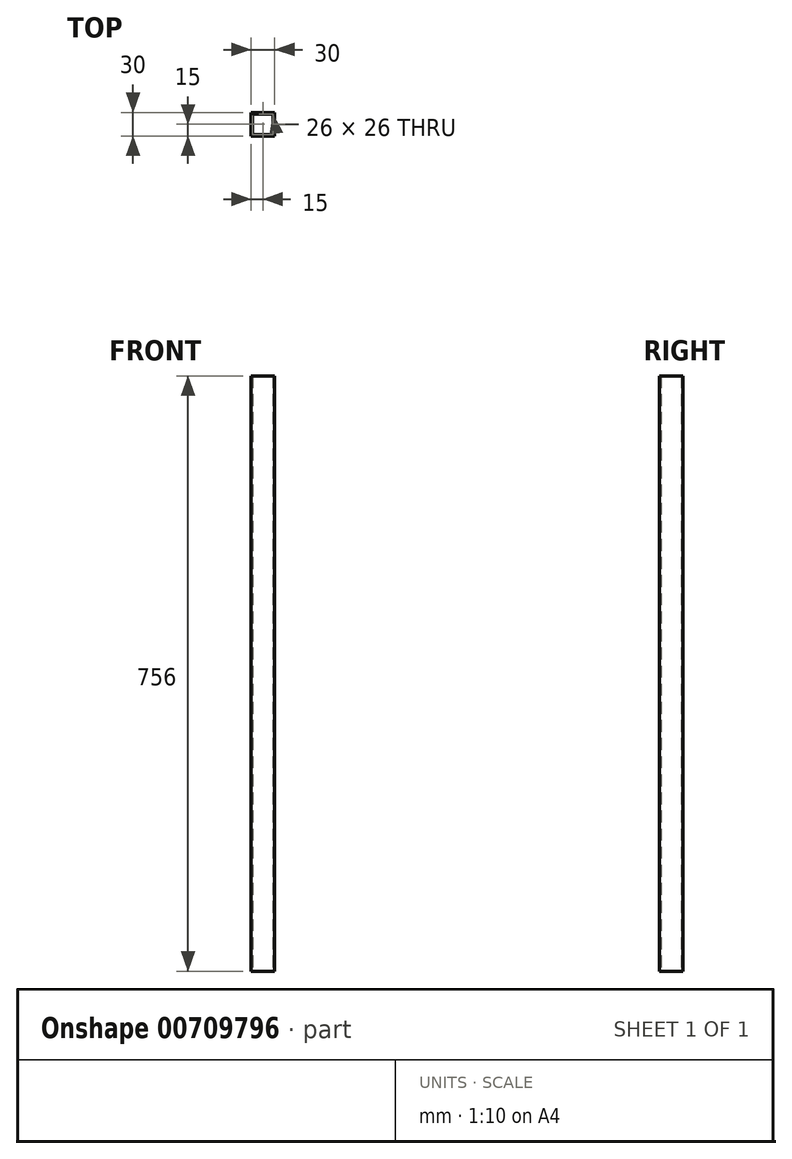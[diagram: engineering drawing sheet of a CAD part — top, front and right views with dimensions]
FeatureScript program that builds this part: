
annotation { "Feature Type Name" : "Feature", "Feature Type Description" : "" }
export const myFeature = defineFeature(function(context is Context, id is Id, definition is map)
    precondition{}
    {
        {
            var Q0;
            Q0=qCreatedBy(makeId("Top.planeOp"),FACE);
            var sketch = newSketch(context, id + "F0", { "sketchPlane" : qUnion([Q0])});
            skLineSegment(sketch, "E0.bottom", {"start": v(0, 0) * mm, "end": v(-30, 0) * mm});
            skLineSegment(sketch, "E0.top", {"start": v(0, 30) * mm, "end": v(-30, 30) * mm});
            skLineSegment(sketch, "E0.left", {"start": v(0, 0) * mm, "end": v(0, 30) * mm});
            skLineSegment(sketch, "E0.right", {"start": v(-30, 0) * mm, "end": v(-30, 30) * mm});
            skLineSegment(sketch, "E1.0", {"start": v(-28, 2) * mm, "end": v(-28, 28) * mm});
            skLineSegment(sketch, "E1.1", {"start": v(-2, 2) * mm, "end": v(-28, 2) * mm});
            skLineSegment(sketch, "E1.2", {"start": v(-2, 2) * mm, "end": v(-2, 28) * mm});
            skLineSegment(sketch, "E1.3", {"start": v(-2, 28) * mm, "end": v(-28, 28) * mm});
            skSolve(sketch);
        }
        {
            var Q0;
            Q0=makeQuery(id+"F0.imprint","IMPRINT",FACE,{"disambiguationData":[TD([[makeQuery(id+"F0.imprint","IMPRINT",EDGE,{"derivedFrom":sQuery(id+"F0.wireOp",EDGE,"E0.bottom")}),-1.0]])]});
            extrude(context, id + "F1", {"entities" : qUnion([Q0]), "depth" : 756 * mm, "offsetDistance" : 25 * mm});
        }
    });
